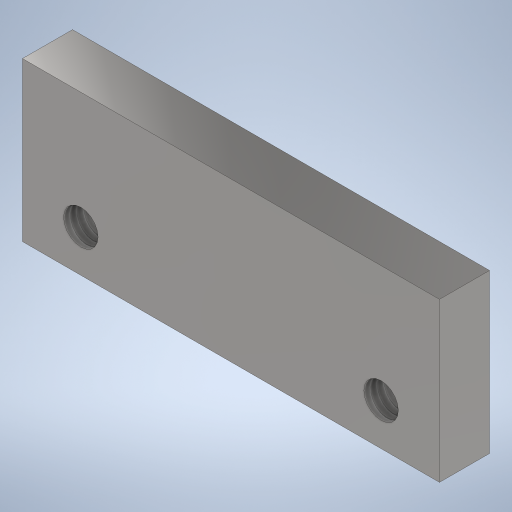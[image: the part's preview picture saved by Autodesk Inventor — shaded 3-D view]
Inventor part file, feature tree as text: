
AUTODESK INVENTOR PART (.ipt)
format: ipt  version: 2023.2 (Build 272271000, 271)  size: 210,944 bytes
history: native  units: mm
features: sketch x2, extrude x1, hole x1
ambient origin geometry x8: Origin, YZ Plane, XZ Plane, XY Plane, X Axis, Y Axis, Z Axis, Center Point
bodies: Solid1 (feature_tree)
feature tree (4):
  extrude  "Extrusion1"  Depth=19.0mm
  hole  "Hole1"  [1 undecoded]
  sketch  "Sketch1"  dims[d0=50.0mm d1=19.0mm]
  sketch  "Sketch2"  dims[d2=6.0mm d3=0.0mm d4=5.0mm d5=5.0mm d6=7.0mm d7=7.0mm d8=4.134mm d9=6.0mm d10=19.05mm d11=4.775mm d12=14.3117mm d13=6.0mm d14=0.0mm]
note: 1 required parameter value undecoded (feature->parameter linkage not recoverable at this tier; creation-order binding heuristic only, values carry confidence <= 0.55)
